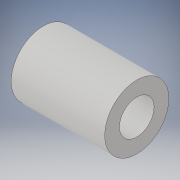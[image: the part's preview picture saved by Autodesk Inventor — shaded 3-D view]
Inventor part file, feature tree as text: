
AUTODESK INVENTOR PART (.ipt)
format: ipt  version: 2019.3 (Build 233278000, 278)  size: 96,256 bytes
history: native  units: in
note: dims shown in document units (in); Inventor stores cm internally (conversion verified against a paired STEP export)
features: extrude x1, sketch x1
ambient origin geometry x8: Origin, YZ Plane, XZ Plane, XY Plane, X Axis, Y Axis, Z Axis, Center Point
bodies: Solid1 (feature_tree)
feature tree (2):
  extrude  "Extrusion1"  Depth=0.73in
  sketch  "Sketch1"  dims[d0=0.5in d1=0.27in d2=0.73in d3=0.0in]
